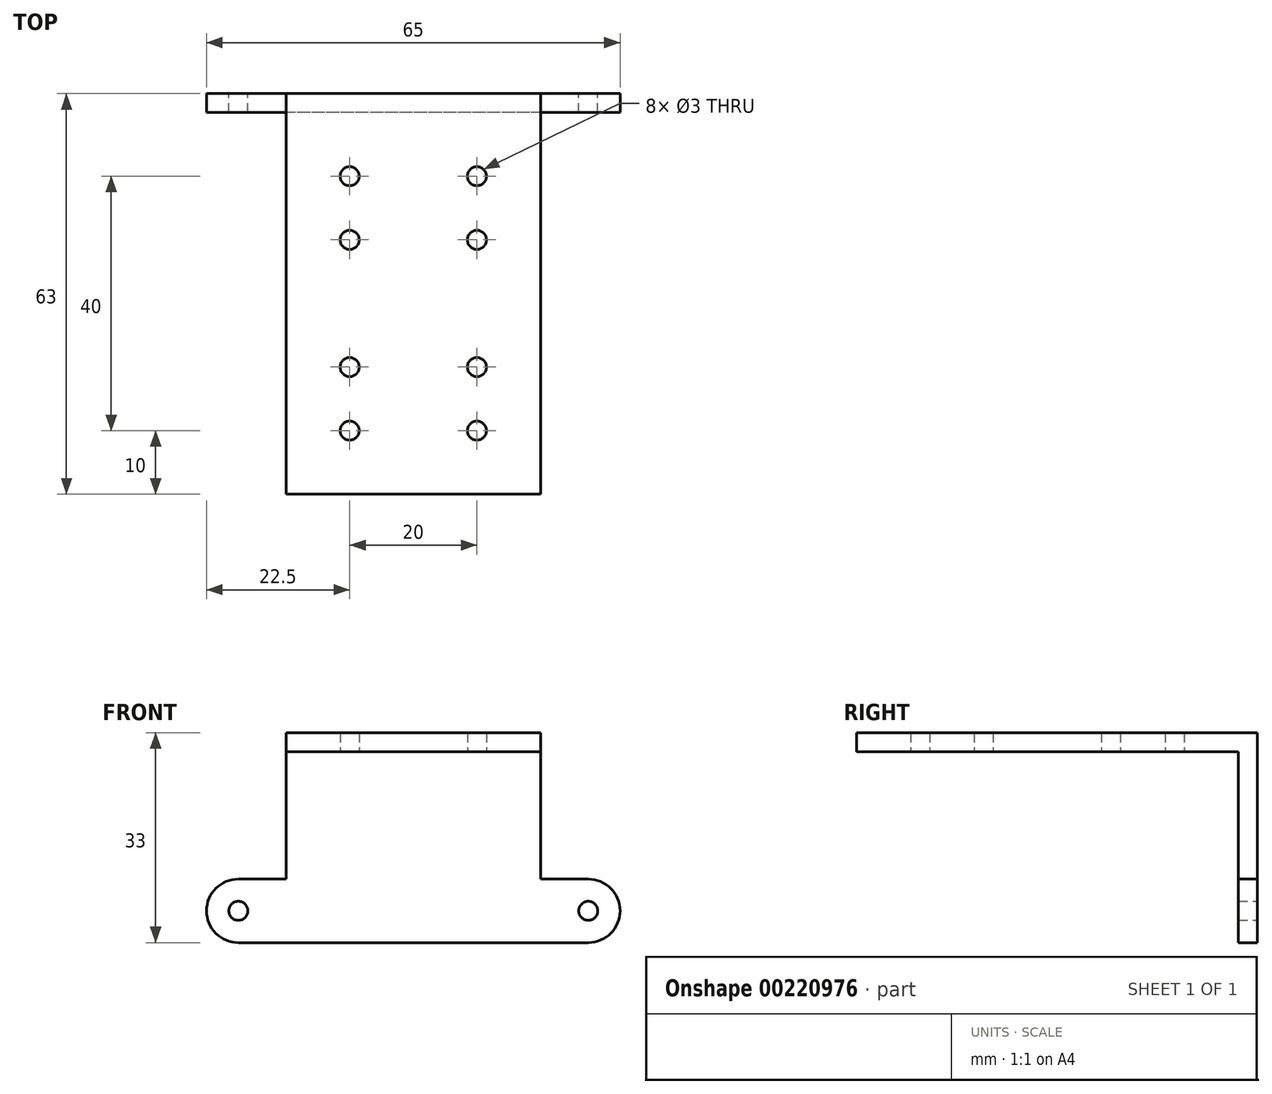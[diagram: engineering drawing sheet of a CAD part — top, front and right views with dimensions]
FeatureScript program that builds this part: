
annotation { "Feature Type Name" : "Feature", "Feature Type Description" : "" }
export const myFeature = defineFeature(function(context is Context, id is Id, definition is map)
    precondition{}
    {
        {
            var Q0;
            Q0=qCreatedBy(makeId("Front.planeOp"),FACE);
            var sketch = newSketch(context, id + "F0", { "sketchPlane" : qUnion([Q0])});
            skLineSegment(sketch, "E0", {"start": v(50, 5) * mm, "end": v(50, 25) * mm});
            skLineSegment(sketch, "E1", {"start": v(50, 25) * mm, "end": v(10, 25) * mm});
            skLineSegment(sketch, "E2", {"start": v(10, 25) * mm, "end": v(10, 5) * mm});
            skLineSegment(sketch, "E3", {"start": v(2.5, 5) * mm, "end": v(10, 5) * mm});
            skLineSegment(sketch, "E4", {"start": v(57.5, 5) * mm, "end": v(50, 5) * mm});
            skArc(sketch, "E5", {"start": v(2.5, 5) * mm, "mid": v(-2.5, 0) * mm, "end": v(2.5, -5) * mm});
            skArc(sketch, "E6", {"start": v(57.5, 5) * mm, "mid": v(62.5, 0) * mm, "end": v(57.5, -5) * mm});
            skLineSegment(sketch, "E7", {"start": v(57.5, -5) * mm, "end": v(2.5, -5) * mm});
            skCircle(sketch, "E8", {"center": v(2.5, 0) * mm, "radius": 1.5 * mm});
            skCircle(sketch, "E9", {"center": v(57.5, 0) * mm, "radius": 1.5 * mm});
            skSolve(sketch);
        }
        {
            var Q0;
            Q0=makeQuery(id+"F0.imprint","IMPRINT",FACE,{"disambiguationData":[TD([[makeQuery(id+"F0.imprint","IMPRINT",EDGE,{"derivedFrom":sQuery(id+"F0.wireOp",EDGE,"2xQEmBC1-Y5n9-HGXJ-f6e7-lHBJXJ514OB0")}),-1.0]])]});
            var Q1;
            Q1=makeQuery(id+"F0.imprint","IMPRINT",FACE,{"disambiguationData":[TD([[makeQuery(id+"F0.imprint","IMPRINT",EDGE,{"derivedFrom":sQuery(id+"F0.wireOp",EDGE,"E0")}),1.0]])]});
            extrude(context, id + "F1", {"entities" : qUnion([Q0, Q1]), "depth" : 3 * mm});
        }
        {
            var Q0;
            Q0=makeQuery(id+"F1.opExtrude","SWEPT_FACE",FACE,{"disambiguationData":[OSD([sQuery(id+"F0.wireOp",EDGE,"E1")])]});
            var sketch = newSketch(context, id + "F2", { "sketchPlane" : qUnion([Q0])});
            skLineSegment(sketch, "E10.bottom", {"start": v(10, 0) * mm, "end": v(50, 0) * mm});
            skLineSegment(sketch, "E10.left", {"start": v(10, 0) * mm, "end": v(10, -3) * mm});
            skLineSegment(sketch, "E10.right", {"start": v(50, 0) * mm, "end": v(50, -3) * mm});
            skLineSegment(sketch, "E11", {"start": v(10, -3) * mm, "end": v(10, -13) * mm});
            skLineSegment(sketch, "E12", {"start": v(10, -13) * mm, "end": v(20, -13) * mm});
            skLineSegment(sketch, "E13", {"start": v(10, -13) * mm, "end": v(10, -23) * mm});
            skLineSegment(sketch, "E14", {"start": v(10, -23) * mm, "end": v(10, -33) * mm});
            skLineSegment(sketch, "E15", {"start": v(10, -33) * mm, "end": v(10, -43) * mm});
            skLineSegment(sketch, "E16", {"start": v(10, -23) * mm, "end": v(20, -23) * mm});
            skLineSegment(sketch, "E17", {"start": v(10, -43) * mm, "end": v(10, -53) * mm});
            skLineSegment(sketch, "E18", {"start": v(10, -43) * mm, "end": v(20, -43) * mm});
            skLineSegment(sketch, "E19", {"start": v(10, -53) * mm, "end": v(20, -53) * mm});
            skLineSegment(sketch, "E20", {"start": v(10, -53) * mm, "end": v(10, -63) * mm});
            skLineSegment(sketch, "E21", {"start": v(50, -3) * mm, "end": v(50, -13) * mm});
            skLineSegment(sketch, "E22", {"start": v(50, -13) * mm, "end": v(50, -23) * mm});
            skLineSegment(sketch, "E23", {"start": v(50, -23) * mm, "end": v(50, -33) * mm});
            skLineSegment(sketch, "E24", {"start": v(50, -33) * mm, "end": v(50, -43) * mm});
            skLineSegment(sketch, "E25", {"start": v(50, -43) * mm, "end": v(50, -53) * mm});
            skLineSegment(sketch, "E26", {"start": v(50, -53) * mm, "end": v(50, -63) * mm});
            skLineSegment(sketch, "E27", {"start": v(50, -63) * mm, "end": v(10, -63) * mm});
            skLineSegment(sketch, "E28", {"start": v(50, -13) * mm, "end": v(40, -13) * mm});
            skLineSegment(sketch, "E29", {"start": v(50, -23) * mm, "end": v(40, -23) * mm});
            skLineSegment(sketch, "E30", {"start": v(50, -43) * mm, "end": v(40, -43) * mm});
            skLineSegment(sketch, "E31", {"start": v(50, -53) * mm, "end": v(40, -53) * mm});
            skCircle(sketch, "E32", {"center": v(20, -13) * mm, "radius": 1.5 * mm});
            skCircle(sketch, "E33", {"center": v(20, -23) * mm, "radius": 1.5 * mm});
            skCircle(sketch, "E34", {"center": v(20, -43) * mm, "radius": 1.5 * mm});
            skCircle(sketch, "E35", {"center": v(20, -53) * mm, "radius": 1.5 * mm});
            skCircle(sketch, "E36", {"center": v(40, -53) * mm, "radius": 1.5 * mm});
            skCircle(sketch, "E37", {"center": v(40, -43) * mm, "radius": 1.5 * mm});
            skCircle(sketch, "E38", {"center": v(40, -23) * mm, "radius": 1.5 * mm});
            skCircle(sketch, "E39", {"center": v(40, -13) * mm, "radius": 1.5 * mm});
            skSolve(sketch);
        }
        {
            var Q0;
            Q0 = qSketchRegion(id + "F2", true);
            extrude(context, id + "F3", {"entities" : qUnion([Q0]), "operationType" : NewBodyOperationType.ADD, "depth" : 3 * mm});
        }
    });
